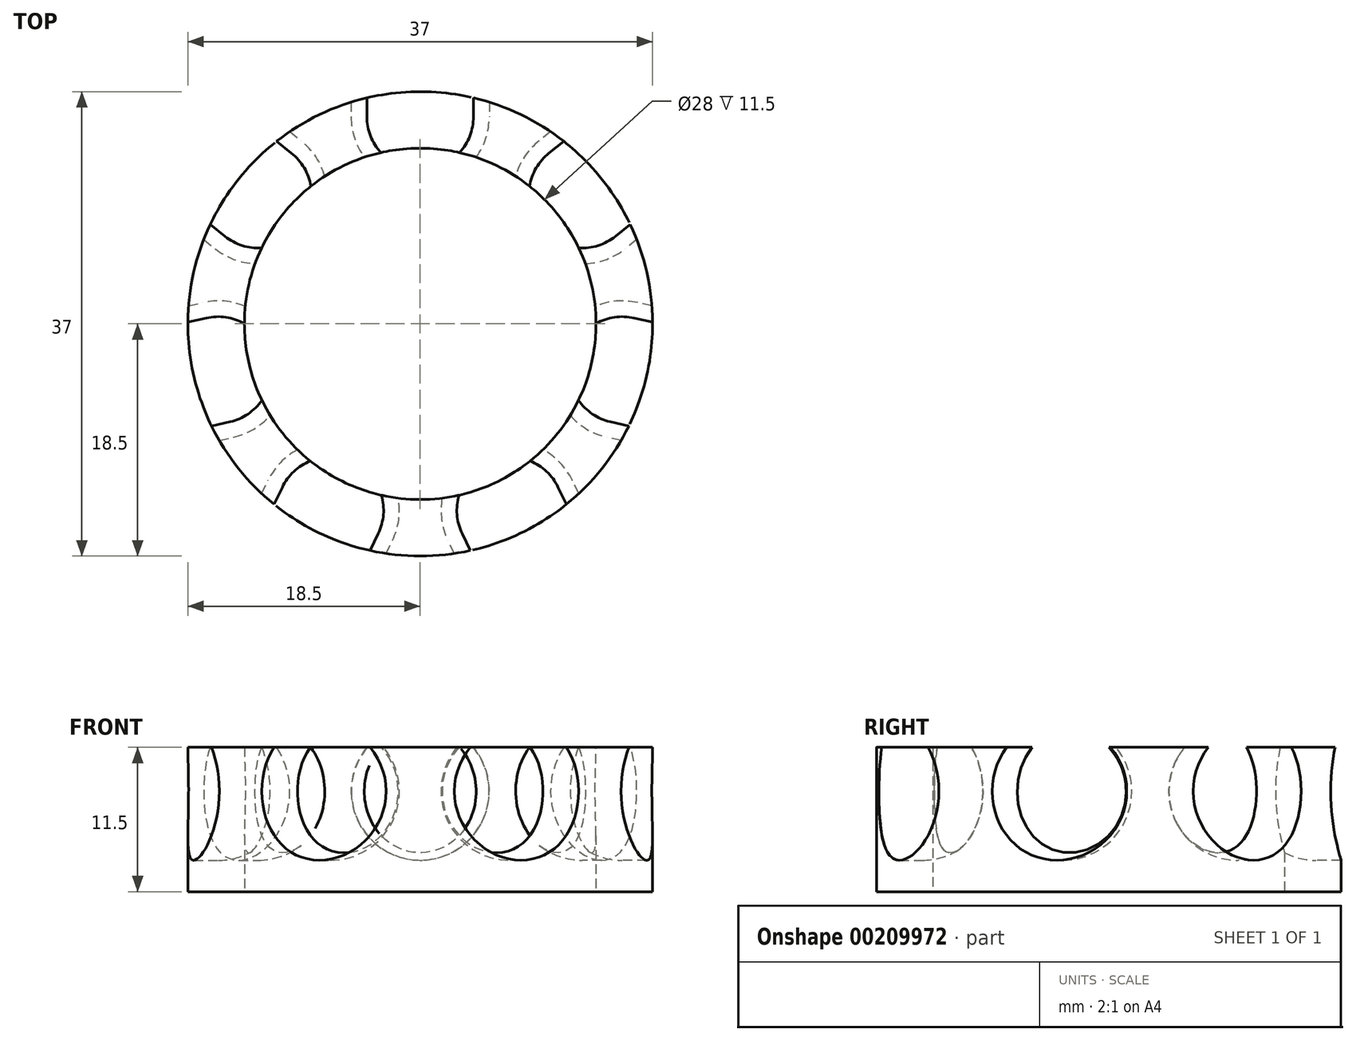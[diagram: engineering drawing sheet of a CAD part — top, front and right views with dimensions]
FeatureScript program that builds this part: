
annotation { "Feature Type Name" : "Feature", "Feature Type Description" : "" }
export const myFeature = defineFeature(function(context is Context, id is Id, definition is map)
    precondition{}
    {
        {
            var Q0;
            Q0=qCreatedBy(makeId("Top.planeOp"),FACE);
            var sketch = newSketch(context, id + "F0", { "sketchPlane" : qUnion([Q0])});
            skCircle(sketch, "E0", {"center": v(0, 0) * mm, "radius": 14 * mm});
            skCircle(sketch, "E1", {"center": v(0, 0) * mm, "radius": 18.5 * mm});
            skSolve(sketch);
        }
        {
            var Q0;
            Q0=makeQuery(id+"F0.imprint","IMPRINT",FACE,{"disambiguationData":[TD([[makeQuery(id+"F0.imprint","IMPRINT",EDGE,{"derivedFrom":sQuery(id+"F0.wireOp",EDGE,"E0")}),-1.0]])]});
            extrude(context, id + "F1", {"entities" : qUnion([Q0]), "depth" : 11.5 * mm});
        }
        {
            var Q0;
            Q0=qCreatedBy(makeId("Top.planeOp"),FACE);
            cPlane(context, id + "F2", {"entities" : qUnion([Q0]), "cplaneType" : CPlaneType.OFFSET, "offset" : 8 * mm, "width" : 150 * mm, "height" : 150 * mm});
        }
        {
            var Q0;
            Q0=qCreatedBy(id+"F2.planeOp",FACE);
            var sketch = newSketch(context, id + "F3", { "sketchPlane" : qUnion([Q0])});
            skCircle(sketch, "E2", {"center": v(0, 0) * mm, "radius": 16.5 * mm});
            skCircle(sketch, "E3", {"center": v(0, 16.5) * mm, "radius": 5.5 * mm});
            skLineSegment(sketch, "E4", {"start": v(-5.5, 16.5) * mm, "end": v(5.5, 16.5) * mm});
            skSolve(sketch);
        }
        {
            var Q0;
            {var subQ0=sQuery(id+"F3.wireOp",EDGE,"E4");var subQ1=sQuery(id+"F3.wireOp",EDGE,"E3");var subQ2=makeQuery(id+"F3.imprint","INTERSECT",VERTEX,{"disambiguationData":[OD(0.0)],"derivedFrom":[subQ1,subQ0]});Q0=makeQuery(id+"F3.imprint","IMPRINT",FACE,{"disambiguationData":[TD([[makeQuery(id+"F3.imprint","IMPRINT",EDGE,{"disambiguationData":[TD([[subQ2,1.0]])],"derivedFrom":subQ1}),1.0]])]});}
            var Q1;
            Q1=sQuery(id+"F3.wireOp",EDGE,"E4");
            revolve(context, id + "F4", {"entities" : qUnion([Q0]), "axis" : qUnion([Q1]), "revolveType" : RevolveType.FULL});
        }
        {
            var Q0;
            Q0=qCreatedBy(makeId("Right.planeOp"),FACE);
            var sketch = newSketch(context, id + "F5", { "sketchPlane" : qUnion([Q0])});
            skLineSegment(sketch, "E5", {"start": v(0, 0) * mm, "end": v(0, 19.97) * mm});
            skSolve(sketch);
        }
        {
            var Q0;
            Q0=makeQuery(id+"F4.opRevolve","SWEPT_BODY",BODY,{"disambiguationData":[OSD([sQuery(id+"F3.wireOp",EDGE,"E3"),sQuery(id+"F3.wireOp",EDGE,"E4")])]});
            var Q1;
            Q1=sQuery(id+"F5.wireOp",EDGE,"E5");
            circularPattern(context, id + "F6", {"operationType" : NewBodyOperationType.REMOVE, "entities" : qUnion([Q0]), "axis" : qUnion([Q1]), "angle" : 360 * degree, "instanceCount" : 7, "equalSpace" : true});
        }
        {
            var Q0;
            Q0=qCreatedBy(makeId("Front.planeOp"),FACE);
            cPlane(context, id + "F7", {"entities" : qUnion([Q0]), "cplaneType" : CPlaneType.OFFSET, "offset" : 16.5 * mm, "oppositeDirection" : true, "width" : 150 * mm, "height" : 150 * mm});
        }
        {
            var Q0;
            Q0=qCreatedBy(id+"F7.planeOp",FACE);
            var sketch = newSketch(context, id + "F8", { "sketchPlane" : qUnion([Q0])});
            skLineSegment(sketch, "E6", {"start": v(0, 0) * mm, "end": v(0, 8) * mm});
            skCircle(sketch, "E7", {"center": v(0, 8) * mm, "radius": 5.5 * mm});
            skSolve(sketch);
        }
        {
            var Q0;
            Q0 = qSketchRegion(id + "F8", true);
            extrude(context, id + "F9", {"entities" : qUnion([Q0]), "oppositeDirection" : true, "depth" : 25 * mm});
        }
        {
            var Q0;
            Q0=makeQuery(id+"F9.opExtrude","SWEPT_BODY",BODY,{"disambiguationData":[OSD([sQuery(id+"F8.wireOp",EDGE,"E7")])]});
            var Q1;
            Q1=sQuery(id+"F5.wireOp",EDGE,"E5");
            circularPattern(context, id + "F10", {"operationType" : NewBodyOperationType.REMOVE, "entities" : qUnion([Q0]), "axis" : qUnion([Q1]), "angle" : 360 * degree, "instanceCount" : 7, "equalSpace" : true});
        }
    });
